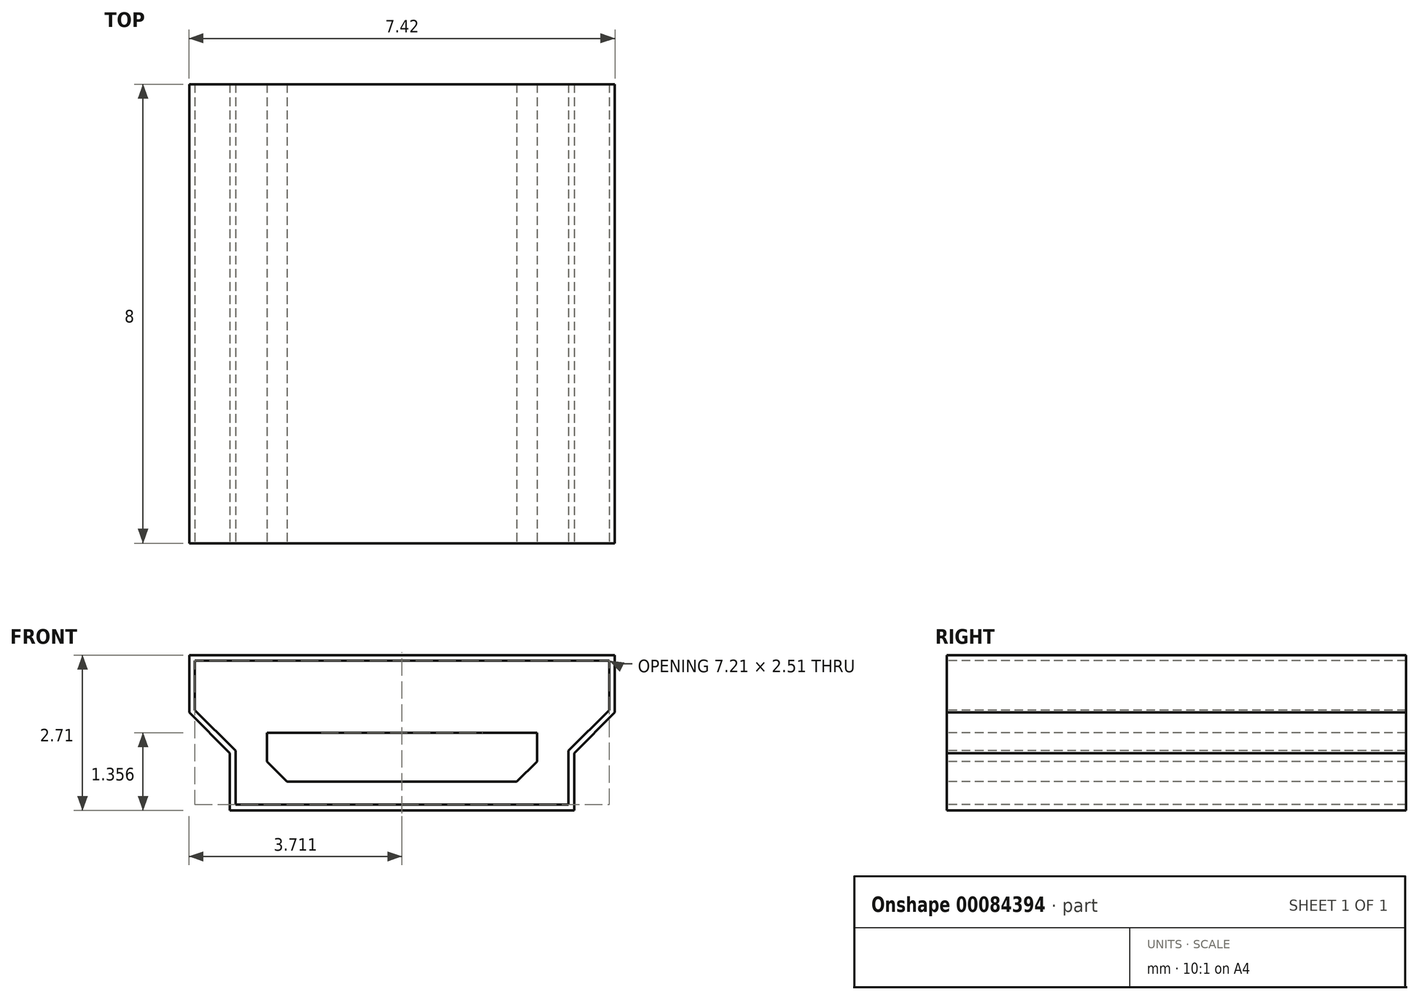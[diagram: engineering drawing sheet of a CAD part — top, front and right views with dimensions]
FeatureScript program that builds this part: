
annotation { "Feature Type Name" : "Feature", "Feature Type Description" : "" }
export const myFeature = defineFeature(function(context is Context, id is Id, definition is map)
    precondition{}
    {
        {
            var Q0;
            Q0=qCreatedBy(makeId("Front.planeOp"),FACE);
            var sketch = newSketch(context, id + "F0", { "sketchPlane" : qUnion([Q0])});
            skLineSegment(sketch, "E0", {"start": v(1.96, 26.91) * mm, "end": v(7.96, 26.91) * mm});
            skLineSegment(sketch, "E1", {"start": v(7.96, 26.91) * mm, "end": v(7.96, 26.91) * mm});
            skLineSegment(sketch, "E2", {"start": v(7.96, 27.91) * mm, "end": v(7.96, 26.91) * mm});
            skLineSegment(sketch, "E3", {"start": v(1.96, 26.91) * mm, "end": v(1.96, 27.91) * mm});
            skLineSegment(sketch, "E4", {"start": v(1.96, 27.91) * mm, "end": v(1.25, 28.62) * mm});
            skLineSegment(sketch, "E5", {"start": v(7.96, 27.91) * mm, "end": v(8.67, 28.62) * mm});
            skLineSegment(sketch, "E6", {"start": v(1.25, 28.62) * mm, "end": v(1.25, 29.62) * mm});
            skLineSegment(sketch, "E7", {"start": v(8.67, 28.62) * mm, "end": v(8.67, 29.62) * mm});
            skLineSegment(sketch, "E8", {"start": v(1.25, 29.62) * mm, "end": v(8.67, 29.62) * mm});
            skSolve(sketch);
        }
        {
            var Q0;
            Q0=makeQuery(id+"F0.imprint","IMPRINT",FACE,{"disambiguationData":[TD([[makeQuery(id+"F0.imprint","IMPRINT",EDGE,{"derivedFrom":sQuery(id+"F0.wireOp",EDGE,"E0")}),1.0]])]});
            extrude(context, id + "F1", {"entities" : qUnion([Q0]), "oppositeDirection" : true, "depth" : 8 * mm});
        }
        {
            var Q0;
            Q0=makeQuery(id+"F1.opExtrude","CAP_FACE",FACE,{"disambiguationData":[OSD([sQuery(id+"F0.wireOp",EDGE,"E0"),sQuery(id+"F0.wireOp",EDGE,"E2"),sQuery(id+"F0.wireOp",EDGE,"E3"),sQuery(id+"F0.wireOp",EDGE,"E4"),sQuery(id+"F0.wireOp",EDGE,"E5"),sQuery(id+"F0.wireOp",EDGE,"E6"),sQuery(id+"F0.wireOp",EDGE,"E7"),sQuery(id+"F0.wireOp",EDGE,"E8")])],"isStart":true});
            var sketch = newSketch(context, id + "F2", { "sketchPlane" : qUnion([Q0])});
            skLineSegment(sketch, "E9", {"start": v(2.06, 27.95) * mm, "end": v(2.06, 27.01) * mm});
            skLineSegment(sketch, "E10", {"start": v(2.06, 27.01) * mm, "end": v(7.86, 27.01) * mm});
            skLineSegment(sketch, "E11", {"start": v(7.86, 27.01) * mm, "end": v(7.86, 27.95) * mm});
            skLineSegment(sketch, "E12", {"start": v(7.86, 27.95) * mm, "end": v(8.57, 28.66) * mm});
            skLineSegment(sketch, "E13", {"start": v(8.57, 28.66) * mm, "end": v(8.57, 29.52) * mm});
            skLineSegment(sketch, "E14", {"start": v(2.06, 27.95) * mm, "end": v(1.35, 28.66) * mm});
            skLineSegment(sketch, "E15", {"start": v(1.35, 28.66) * mm, "end": v(1.35, 29.52) * mm});
            skLineSegment(sketch, "E16", {"start": v(1.35, 29.52) * mm, "end": v(8.57, 29.52) * mm});
            skLineSegment(sketch, "E17", {"start": v(2.96, 27.41) * mm, "end": v(6.96, 27.41) * mm});
            skLineSegment(sketch, "E18", {"start": v(2.96, 27.41) * mm, "end": v(2.6, 27.77) * mm});
            skLineSegment(sketch, "E19", {"start": v(6.96, 27.41) * mm, "end": v(7.31, 27.77) * mm});
            skLineSegment(sketch, "E20", {"start": v(2.6, 27.77) * mm, "end": v(2.6, 28.27) * mm});
            skLineSegment(sketch, "E21", {"start": v(7.31, 27.77) * mm, "end": v(7.31, 28.27) * mm});
            skLineSegment(sketch, "E22", {"start": v(2.6, 28.27) * mm, "end": v(7.31, 28.27) * mm});
            skSolve(sketch);
        }
        {
            var Q0;
            Q0=makeQuery(id+"F2.imprint","IMPRINT",FACE,{"disambiguationData":[TD([[makeQuery(id+"F2.imprint","IMPRINT",EDGE,{"derivedFrom":sQuery(id+"F2.wireOp",EDGE,"E9")}),1.0]])]});
            extrude(context, id + "F3", {"entities" : qUnion([Q0]), "operationType" : NewBodyOperationType.REMOVE, "oppositeDirection" : true, "depth" : 8 * mm});
        }
    });
